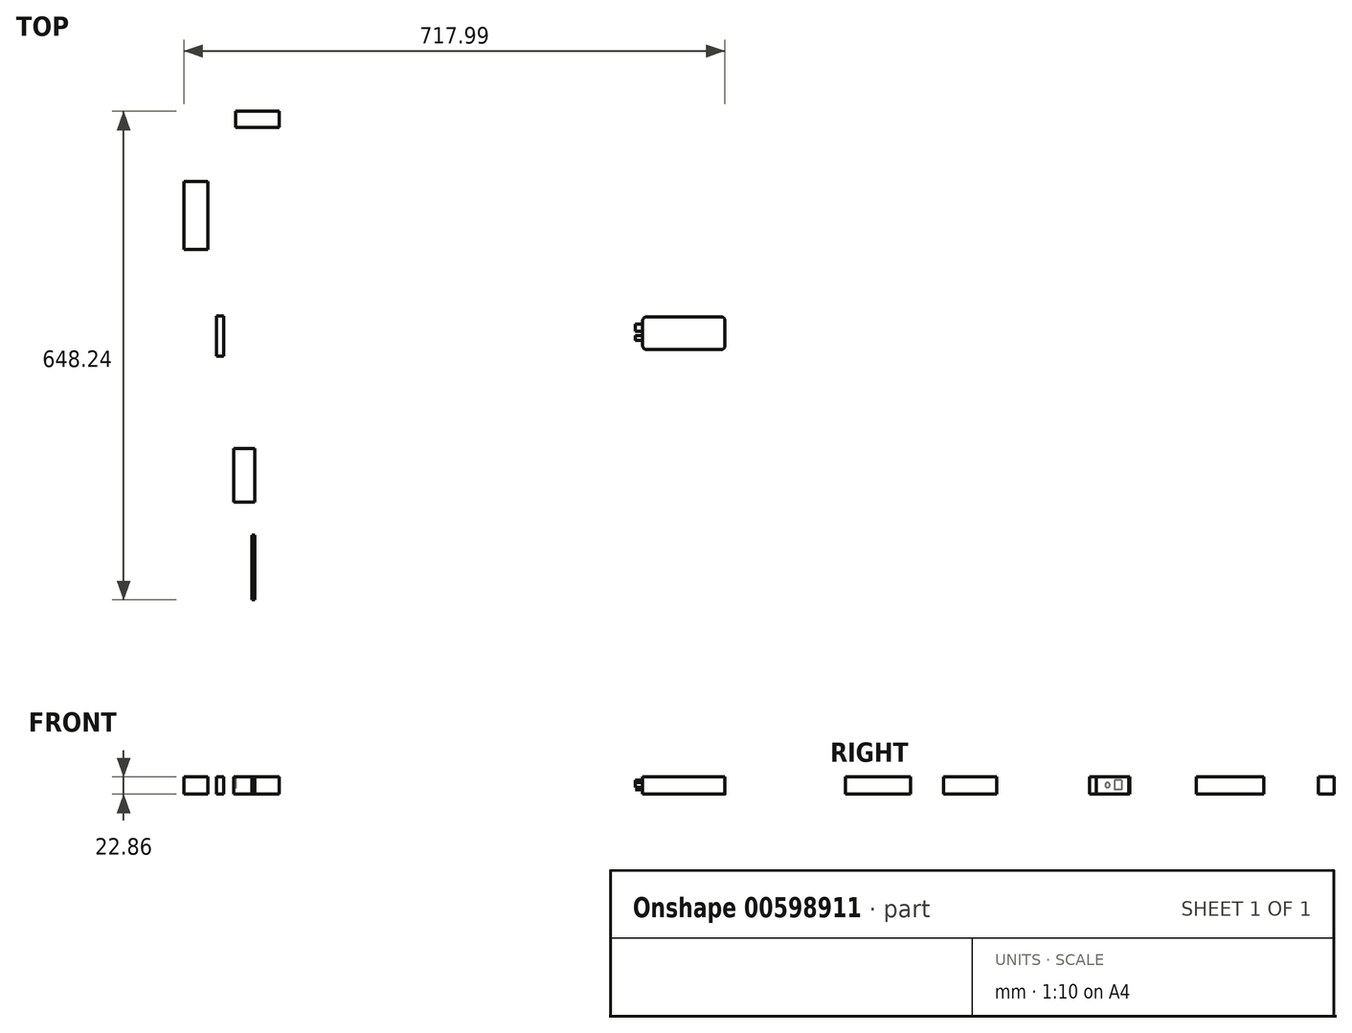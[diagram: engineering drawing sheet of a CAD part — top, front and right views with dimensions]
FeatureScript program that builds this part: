
annotation { "Feature Type Name" : "Feature", "Feature Type Description" : "" }
export const myFeature = defineFeature(function(context is Context, id is Id, definition is map)
    precondition{}
    {
        {
            var Q0;
            Q0=qCreatedBy(makeId("Top.planeOp"),FACE);
            var sketch = newSketch(context, id + "F0", { "sketchPlane" : qUnion([Q0])});
            skLineSegment(sketch, "E0.bottom", {"start": v(-273.37, -316.64) * mm, "end": v(-276.98, -316.64) * mm});
            skLineSegment(sketch, "E0.top", {"start": v(-273.37, -230.53) * mm, "end": v(-276.98, -230.53) * mm});
            skLineSegment(sketch, "E0.left", {"start": v(-273.37, -316.64) * mm, "end": v(-273.37, -230.53) * mm});
            skLineSegment(sketch, "E0.right", {"start": v(-276.98, -316.64) * mm, "end": v(-276.98, -230.53) * mm});
            skLineSegment(sketch, "E1.bottom", {"start": v(-273.37, -186.98) * mm, "end": v(-300.96, -186.98) * mm});
            skLineSegment(sketch, "E1.top", {"start": v(-273.37, -116.09) * mm, "end": v(-300.96, -116.09) * mm});
            skLineSegment(sketch, "E1.left", {"start": v(-273.37, -186.98) * mm, "end": v(-273.37, -116.09) * mm});
            skLineSegment(sketch, "E1.right", {"start": v(-300.96, -186.98) * mm, "end": v(-300.96, -116.09) * mm});
            skLineSegment(sketch, "E2.bottom", {"start": v(-323.9, 6.97) * mm, "end": v(-314.66, 6.97) * mm});
            skLineSegment(sketch, "E2.top", {"start": v(-323.9, 60.4) * mm, "end": v(-314.66, 60.4) * mm});
            skLineSegment(sketch, "E2.left", {"start": v(-323.9, 6.97) * mm, "end": v(-323.9, 60.4) * mm});
            skLineSegment(sketch, "E2.right", {"start": v(-314.66, 6.97) * mm, "end": v(-314.66, 60.4) * mm});
            skLineSegment(sketch, "E3.bottom", {"start": v(-335.51, 148.6) * mm, "end": v(-367.35, 148.6) * mm});
            skLineSegment(sketch, "E3.top", {"start": v(-335.51, 238.45) * mm, "end": v(-367.35, 238.45) * mm});
            skLineSegment(sketch, "E3.left", {"start": v(-335.51, 148.6) * mm, "end": v(-335.51, 238.45) * mm});
            skLineSegment(sketch, "E3.right", {"start": v(-367.35, 148.6) * mm, "end": v(-367.35, 238.45) * mm});
            skLineSegment(sketch, "E4.bottom", {"start": v(-298.55, 310.24) * mm, "end": v(-240.73, 310.24) * mm});
            skLineSegment(sketch, "E4.top", {"start": v(-298.55, 331.6) * mm, "end": v(-240.73, 331.6) * mm});
            skLineSegment(sketch, "E4.left", {"start": v(-298.55, 310.24) * mm, "end": v(-298.55, 331.6) * mm});
            skLineSegment(sketch, "E4.right", {"start": v(-240.73, 310.24) * mm, "end": v(-240.73, 331.6) * mm});
            skLineSegment(sketch, "E5.bottom", {"start": v(241.42, 58.75) * mm, "end": v(350.64, 58.75) * mm});
            skLineSegment(sketch, "E5.top", {"start": v(241.42, 15.57) * mm, "end": v(350.64, 15.57) * mm});
            skLineSegment(sketch, "E5.left", {"start": v(241.42, 58.75) * mm, "end": v(241.42, 15.57) * mm});
            skLineSegment(sketch, "E5.right", {"start": v(350.64, 58.75) * mm, "end": v(350.64, 15.57) * mm});
            skSolve(sketch);
        }
        {
            var Q0;
            Q0 = qSketchRegion(id + "F0", true);
            extrude(context, id + "F1", {"entities" : qUnion([Q0]), "depth" : 22.86 * mm, "offsetDistance" : 25.4 * mm});
        }
        {
            var Q0;
            Q0=makeQuery(id+"F1.opExtrude","SWEPT_EDGE",EDGE,{"disambiguationData":[OSD([sQuery(id+"F0.wireOp",EDGE,"E5.top"),sQuery(id+"F0.wireOp",EDGE,"E5.right")])]});
            var Q1;
            Q1=makeQuery(id+"F1.opExtrude","SWEPT_EDGE",EDGE,{"disambiguationData":[OSD([sQuery(id+"F0.wireOp",EDGE,"E5.bottom"),sQuery(id+"F0.wireOp",EDGE,"E5.right")])]});
            var Q2;
            Q2=makeQuery(id+"F1.opExtrude","SWEPT_EDGE",EDGE,{"disambiguationData":[OSD([sQuery(id+"F0.wireOp",EDGE,"E5.top"),sQuery(id+"F0.wireOp",EDGE,"E5.left")])]});
            var Q3;
            Q3=makeQuery(id+"F1.opExtrude","SWEPT_EDGE",EDGE,{"disambiguationData":[OSD([sQuery(id+"F0.wireOp",EDGE,"E5.bottom"),sQuery(id+"F0.wireOp",EDGE,"E5.left")])]});
            fillet(context, id + "F2", {"entities" : qUnion([Q0, Q1, Q2, Q3]), "radius" : 5.08 * mm, "tangentPropagation" : true, "allowEdgeOverflow" : false});
        }
        {
            var Q0;
            Q0=makeQuery(id+"F1.opExtrude","SWEPT_FACE",FACE,{"disambiguationData":[OSD([sQuery(id+"F0.wireOp",EDGE,"E5.left")])]});
            var sketch = newSketch(context, id + "F3", { "sketchPlane" : qUnion([Q0])});
            skLineSegment(sketch, "E6.bottom", {"start": v(-49.22, 18.41) * mm, "end": v(-39.7, 18.41) * mm});
            skLineSegment(sketch, "E6.top", {"start": v(-49.22, 5.71) * mm, "end": v(-39.7, 5.71) * mm});
            skLineSegment(sketch, "E6.left", {"start": v(-49.22, 18.41) * mm, "end": v(-49.22, 5.71) * mm});
            skLineSegment(sketch, "E6.right", {"start": v(-39.7, 18.41) * mm, "end": v(-39.7, 5.71) * mm});
            skCircle(sketch, "E7", {"center": v(-30.8, 12.07) * mm, "radius": 3.18 * mm});
            skPoint(sketch, "E7.centerSnap0", {"position": v(-39.7, 12.06) * mm});
            skSolve(sketch);
        }
        {
            var Q0;
            Q0 = qSketchRegion(id + "F3", true);
            extrude(context, id + "F4", {"entities" : qUnion([Q0]), "operationType" : NewBodyOperationType.ADD, "depth" : 9.52 * mm, "offsetDistance" : 25.4 * mm});
        }
    });
